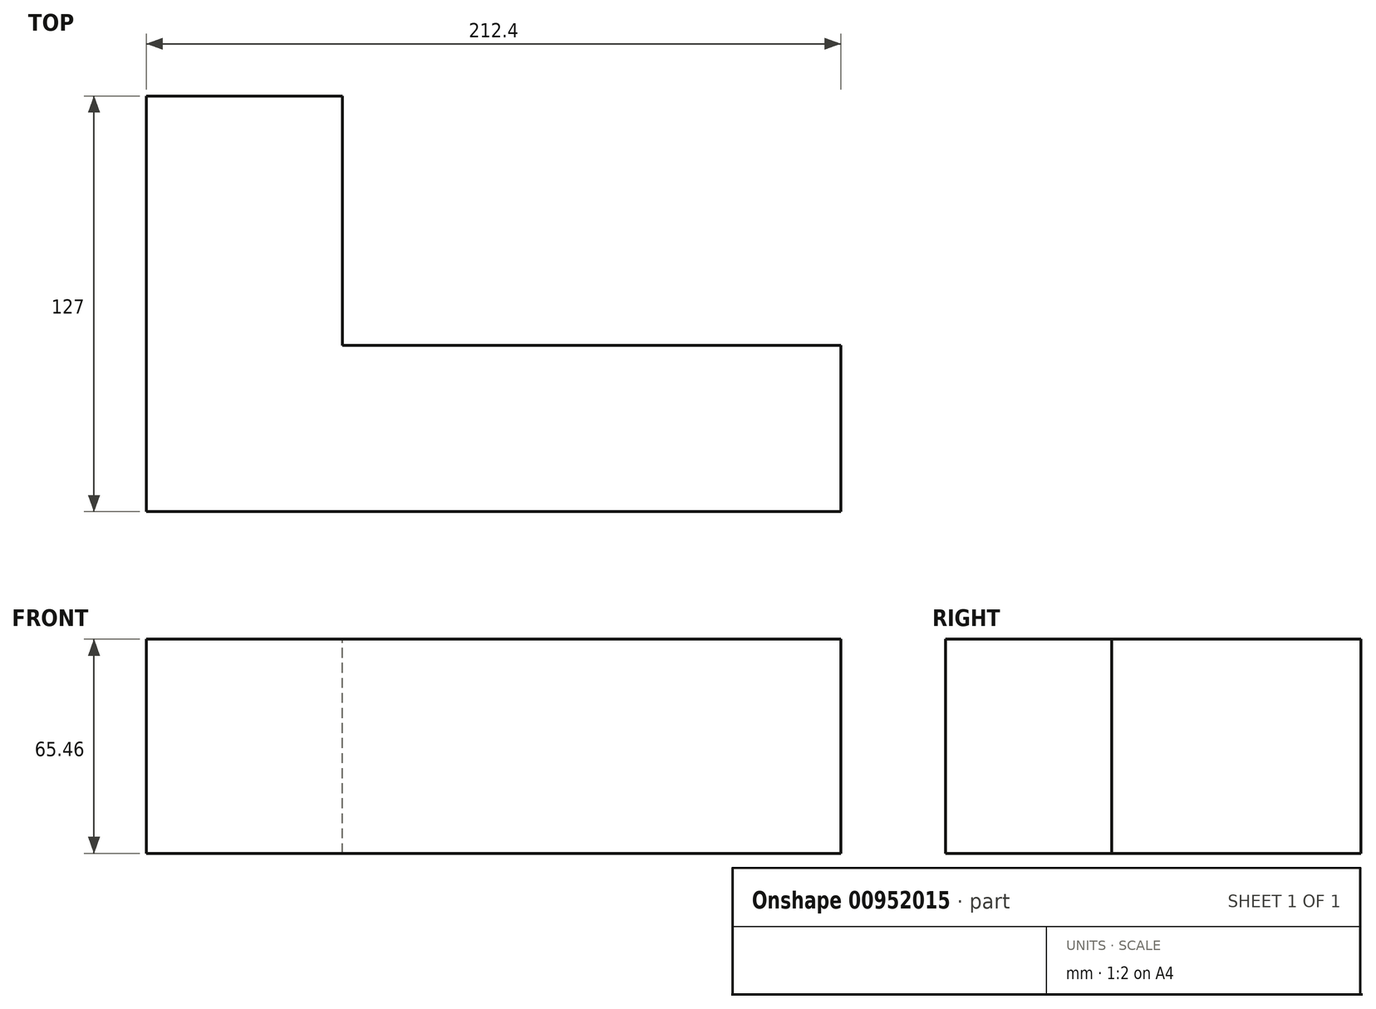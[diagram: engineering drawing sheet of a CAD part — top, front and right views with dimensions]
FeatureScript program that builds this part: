
annotation { "Feature Type Name" : "Feature", "Feature Type Description" : "" }
export const myFeature = defineFeature(function(context is Context, id is Id, definition is map)
    precondition{}
    {
        {
            var Q0;
            Q0=qCreatedBy(makeId("Front.planeOp"),FACE);
            var sketch = newSketch(context, id + "F0", { "sketchPlane" : qUnion([Q0])});
            skLineSegment(sketch, "E0.bottom", {"start": v(0, 0) * mm, "end": v(34.6, 0) * mm});
            skLineSegment(sketch, "E0.top", {"start": v(0, 65.46) * mm, "end": v(34.6, 65.46) * mm});
            skLineSegment(sketch, "E0.left", {"start": v(0, 0) * mm, "end": v(0, 65.46) * mm});
            skLineSegment(sketch, "E0.right", {"start": v(34.6, 0) * mm, "end": v(34.6, 65.46) * mm});
            skSolve(sketch);
        }
        {
            var Q0;
            Q0 = qSketchRegion(id + "F0", true);
            var Q1;
            Q1=makeQuery(id+"F0.imprint","IMPRINT",FACE,{"disambiguationData":[TD([[makeQuery(id+"F0.imprint","IMPRINT",EDGE,{"derivedFrom":sQuery(id+"F0.wireOp",EDGE,"E0.bottom")}),1.0]])]});
            extrude(context, id + "F1", {"entities" : qUnion([Q0, Q1]), "depth" : 50.8 * mm, "offsetDistance" : 25.4 * mm});
        }
        {
            var Q0;
            Q0=makeQuery(id+"F1.opExtrude","SWEPT_FACE",FACE,{"disambiguationData":[OSD([sQuery(id+"F0.wireOp",EDGE,"E0.right")])]});
            extrude(context, id + "F2", {"entities" : qUnion([Q0]), "operationType" : NewBodyOperationType.ADD, "depth" : 152.4 * mm, "offsetDistance" : 25.4 * mm});
        }
        {
            var Q0;
            Q0=makeQuery(id+"F0.imprint","IMPRINT",FACE,{"disambiguationData":[TD([[makeQuery(id+"F0.imprint","IMPRINT",EDGE,{"derivedFrom":sQuery(id+"F0.wireOp",EDGE,"E0.bottom")}),1.0]])]});
            extrude(context, id + "F3", {"entities" : qUnion([Q0]), "operationType" : NewBodyOperationType.ADD, "depth" : -76.2 * mm, "offsetDistance" : 25.4 * mm});
        }
        {
            var Q0;
            {var subQ0=sQuery(id+"F0.wireOp",EDGE,"E0.left");Q0=makeQuery(id+"F3.boolean.opBoolean","MERGE",FACE,{"derivedFrom":[makeQuery(id+"F1.opExtrude","SWEPT_FACE",FACE,{"disambiguationData":[OSD([subQ0])]}),makeQuery(id+"F3.opExtrude","SWEPT_FACE",FACE,{"disambiguationData":[OSD([subQ0])]})]});}
            extrude(context, id + "F4", {"entities" : qUnion([Q0]), "operationType" : NewBodyOperationType.ADD, "depth" : 25.4 * mm, "offsetDistance" : 25.4 * mm});
        }
    });
